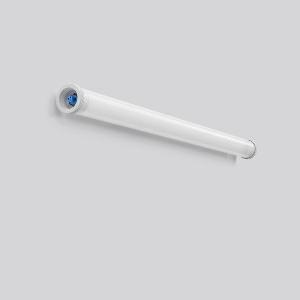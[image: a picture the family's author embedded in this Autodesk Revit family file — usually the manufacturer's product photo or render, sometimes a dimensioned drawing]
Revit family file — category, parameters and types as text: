
# Revit family: planox_tube_601071_002_1_730hf_5701
name_source: partatom
category: Lighting Fixtures
units: mm (PartAtom-declared; Revit-internal decimal feet)

## family parameters
Cut with Voids When Loaded = No
Host = Face
Light Source = No
Part Type = Normal
Room Calculation Point = No
Round Connector Dimension = Use Diameter
Shared = No

## types (1)
- PLANOX TUBE (1 x LED Modul 840, 5350 lm, 4000)
    Apparent Load = 39 VA
    CIE Flux Codes = 42 71 89 90 100
    Color Rendering = 80
    Color Temperature = 4000
    Default Elevation = 1800 mm
    Description = Series: PLANOX TUBE
Robust protective tube luminaire for tough requirements. Rack made of sheet steel, white powder coated. End caps made of plastic (polyamide) grey. Diffuser made of plastic (polycarbonate), opal, shockproof. Symmetrical light distribution. Homogeneous light distribution. With accessories for wall, ceiling or pendant mounting. Suitable for through-wiring. With integrated HF movement sensor. Movement sensor functional parameters: Hold time: can be set with Casambi app. Range: up to 6 m, adjustable in 4 steps. Brightness sensor: adjustable in 5 steps. Factory setting: hold time adjustable via Casambi app, brightness threshold deactivated, detection range 100%. Mounting set must be ordered separately. Luminaire with limited surface temperature in accordance with EN 60598-2-24 for use in environments in which a deposit of conductive dust on the luminaire can be expected. Qualified for use in the food and drink industry. Suitable for lighting in public car parks and public off-street parking spaces according to DIN 67528. Environmentally friendly and resource-saving due to replaceable components. 
Colour: white
Diameter: 78 mm
Length: 1349 mm
Lamp: LED
Socket: without socket
Colour temperature: 4000K
Colour rendering index (CRI): 83
System power: 39 W
Rated luminous flux: 5350 lm
Luminous efficiency: 137 lm/W
Control gear: Dimmable Bluetooth converter
Protection class: I
Type of protection: IP 67
    Height = 0 mm  [stored 0 ft]
    Lamp = 1 x LED Modul 840
    Lamp Light Flux = 5350 lm
    Lamp count = 1
    Length = 1349 mm
    Lifetime = 50000 h
    Luminous efficacy = 137 lm/W
    Manufacturer = RZB
    ModVariant = No
    Model = 601071.002.1.730HF
    Mounting Place = Ceiling, Wall
    Mounting Type = Surface mounted
    Number of Poles = 1
    OnlyDefault = Yes
    Power Factor = 1
    Product Name = PLANOX TUBE
    Product group = Surface mounted luminaires for moist/humid enviroments
    ProductGroupID = 308
    Protection Class = Protection class I
    Protection Degree = Degree of protection
    RLX_Detail_Level = 1
    RLX_Emergency_Light_Flux = 0 lm
    RLX_Emergency_Type = 0
    RLX_Emergency_Type_DB = No
    RlxData = <blob elided: 34001 chars, md5=026e2b40>
    Socket = socket
    Standby Power = 0 W
    System Light Flux = 5350 lm
    System Power = 39 W
    Type Comments = Product without accessories
    Type Image = 601071.002.jpg
    URL = http://relux.com
    VarID = ---
    Voltage = 230 V
    Voltage Range = 220-240 V
    Weight = 0.00 kg
    Width = 0 mm  [stored 0 ft]

note: [stored X ft] marks values corroborated as IEEE doubles in the binary element streams (Revit-internal decimal feet)

## geometry (parser evidence)
native form markers: Blend x4, Sweep x14
no freeform markers — native parametric forms only
